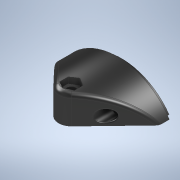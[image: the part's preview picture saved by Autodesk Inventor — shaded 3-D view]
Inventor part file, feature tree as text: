
AUTODESK INVENTOR PART (.ipt)
format: ipt  version: 2020 (Build 240168000, 168)  size: 302,592 bytes
history: native  units: in
note: dims shown in document units (in); Inventor stores cm internally (conversion verified against a paired STEP export)
features: sketch x7, extrude x4, hole x3, revolve x2, fillet x2, plane x1
ambient origin geometry x8: Origin, YZ Plane, XZ Plane, XY Plane, X Axis, Y Axis, Z Axis, Center Point
bodies: Solid1 (feature_tree)
feature tree (19):
  sketch  "Sketch1"  dims[d0=1.85in d1=0.125in]
  revolve  "Revolution1"  [1 undecoded]
  extrude  "Extrusion1"  Depth=0.25in
  extrude  "Extrusion2"  Depth=1.375in
  hole  "Hole1"  [1 undecoded]
  plane  "Work Plane1"
  hole  "Hole2"  [1 undecoded]
  extrude  "Extrusion3"  Depth=0.4475in
  extrude  "Extrusion4"  Depth=0.1875in TaperAngle=0.0deg
  revolve  "Revolution2"  [1 undecoded]
  hole  "Hole4"  [1 undecoded]
  fillet  "Fillet1"  Radius=0.5in
  fillet  "Fillet2"  [1 undecoded]
  sketch  "Sketch2"  dims[d2=1.74in d3=0.25in]
  sketch  "Sketch3"  dims[d4=0.25in d5=1.375in]
  sketch  "Sketch4"  dims[d6=180.0deg d7=1.0in d8=0.0in]
  sketch  "Sketch5"  dims[d9=1.332in d10=0.0in d11=1.5in]
  sketch  "Sketch8"  dims[d12=1.25in]
  sketch  "Sketch9"  dims[d13=0.205in d14=0.75in d15=0.3438in d16=1.0in d17=0.5635in d18=1.0in d19=0.8108in d20=0.266in d21=0.75in d22=0.25in d23=0.25in d24=0.5635in d25=1.0in d26=0.8108in d27=0.4475in d28=0.1875in d29=0.0in d30=3.25in d31=1.0in d32=0.5in d33=0.0in d45=120.0deg d49=1.2in d50=180.0deg d52=0.325in d53=0.5in d54=0.5625in d55=0.35in d56=0.75in d57=0.51in d58=0.188in d59=0.5635in d60=0.25in d61=0.0in d62=0.125in d63=0.0312in d38=1.0in d39=1.0in d40=1.0in d41=0.15in d42=0.25in d43=0.375in d44=0.5635in d46=0.8108in d47=0.0625in d48=0.75in]
note: 6 required parameter values undecoded (feature->parameter linkage not recoverable at this tier; creation-order binding heuristic only, values carry confidence <= 0.55)